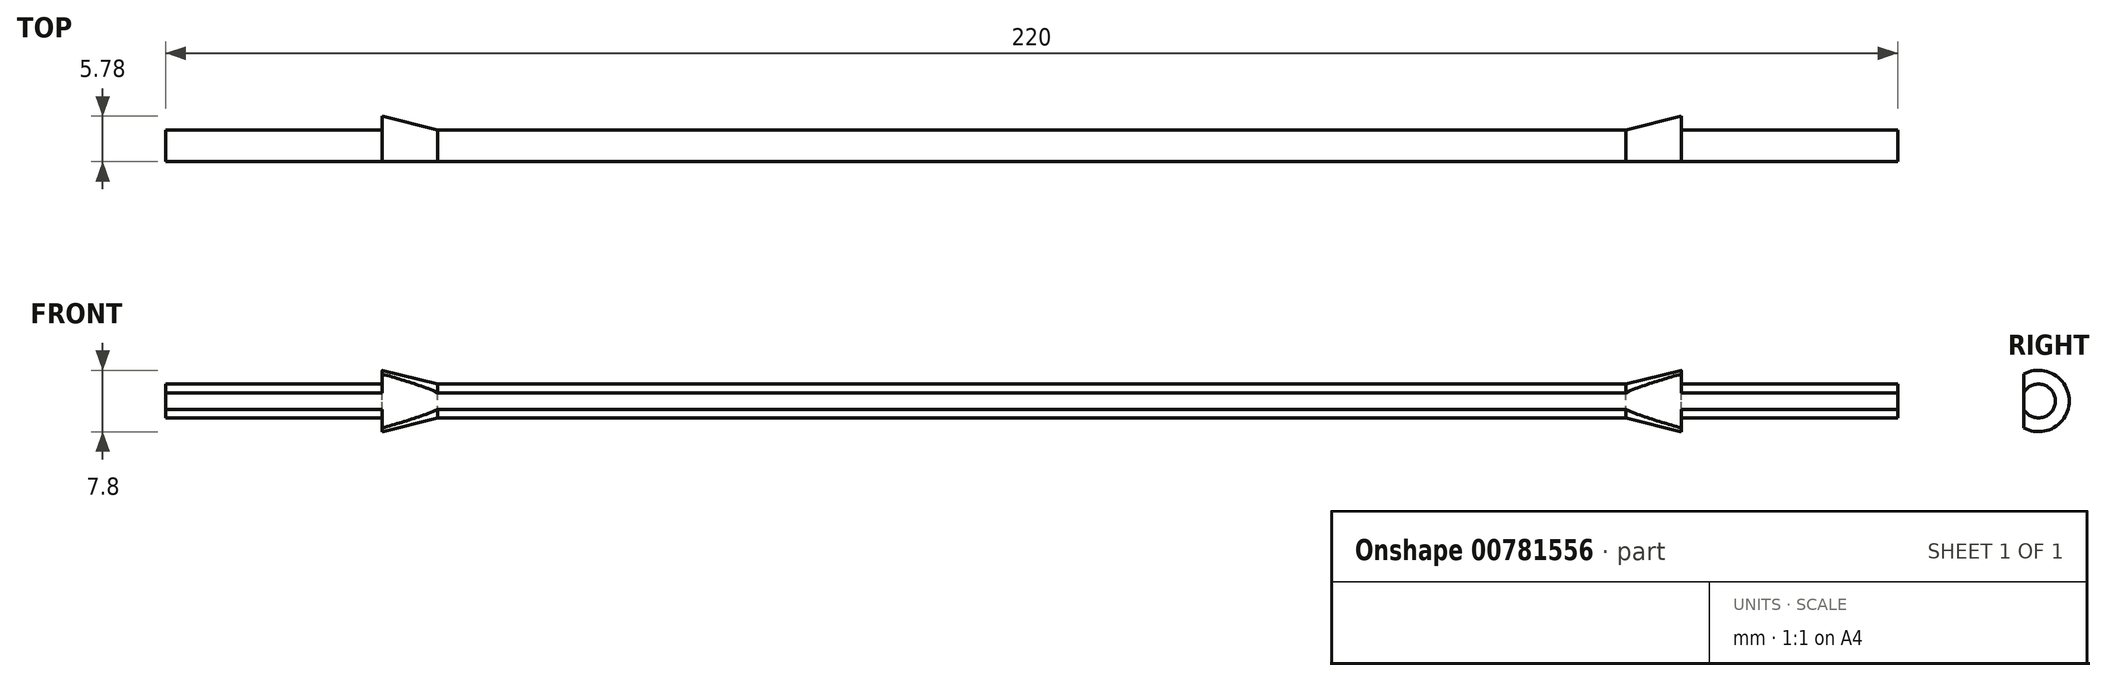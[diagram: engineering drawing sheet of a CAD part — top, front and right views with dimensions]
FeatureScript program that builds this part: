
annotation { "Feature Type Name" : "Feature", "Feature Type Description" : "" }
export const myFeature = defineFeature(function(context is Context, id is Id, definition is map)
    precondition{}
    {
        {
            var Q0;
            Q0=qCreatedBy(makeId("Top.planeOp"),FACE);
            var sketch = newSketch(context, id + "F0", { "sketchPlane" : qUnion([Q0])});
            skLineSegment(sketch, "E0.bottom", {"start": v(-123.69, -1.75) * mm, "end": v(96.31, -1.75) * mm});
            skLineSegment(sketch, "E0.top", {"start": v(-123.69, -6.05) * mm, "end": v(96.31, -6.05) * mm});
            skLineSegment(sketch, "E0.left", {"start": v(-123.69, -1.75) * mm, "end": v(-123.69, -6.05) * mm});
            skLineSegment(sketch, "E0.right", {"start": v(96.31, -1.75) * mm, "end": v(96.31, -6.05) * mm});
            skPoint(sketch, "E1", {"position": v(-13.69, -6.05) * mm});
            skLineSegment(sketch, "E2", {"start": v(-96.19, -7.8) * mm, "end": v(-96.19, 0) * mm});
            skPoint(sketch, "E3", {"position": v(-123.69, -3.9) * mm});
            skPoint(sketch, "E4", {"position": v(96.31, -3.9) * mm});
            skLineSegment(sketch, "E5", {"start": v(96.31, -3.9) * mm, "end": v(-123.69, -3.9) * mm});
            skPoint(sketch, "E6", {"position": v(-96.19, -3.9) * mm});
            skLineSegment(sketch, "E7", {"start": v(-96.19, 0) * mm, "end": v(-80.53, -3.9) * mm});
            skLineSegment(sketch, "E8", {"start": v(-80.53, -3.9) * mm, "end": v(-96.19, -7.8) * mm});
            skLineSegment(sketch, "E9", {"start": v(68.81, 0) * mm, "end": v(68.81, -7.8) * mm});
            skPoint(sketch, "E10", {"position": v(68.81, -3.9) * mm});
            skLineSegment(sketch, "E11", {"start": v(68.81, -7.8) * mm, "end": v(53.15, -3.9) * mm});
            skLineSegment(sketch, "E12", {"start": v(53.15, -3.9) * mm, "end": v(68.81, 0) * mm});
            skLineSegment(sketch, "E13", {"start": v(-123.69, -3.9) * mm, "end": v(-96.19, -3.9) * mm});
            skLineSegment(sketch, "E14", {"start": v(68.81, -3.9) * mm, "end": v(96.31, -3.9) * mm});
            skSolve(sketch);
        }
        {
            var Q0;
            {var subQ0=sQuery(id+"F0.wireOp",EDGE,"E7");var subQ1=sQuery(id+"F0.wireOp",EDGE,"E0.bottom");var subQ2=makeQuery(id+"F0.imprint","INTERSECT",VERTEX,{"derivedFrom":[subQ1,subQ0]});Q0=makeQuery(id+"F0.imprint","IMPRINT",FACE,{"disambiguationData":[TD([[makeQuery(id+"F0.imprint","IMPRINT",EDGE,{"disambiguationData":[TD([[subQ2,-1.0]])],"derivedFrom":subQ1}),-1.0]])]});}
            var Q1;
            {var subQ0=sQuery(id+"F0.wireOp",EDGE,"E7");var subQ1=sQuery(id+"F0.wireOp",EDGE,"E0.bottom");var subQ2=makeQuery(id+"F0.imprint","INTERSECT",VERTEX,{"derivedFrom":[subQ1,subQ0]});Q1=makeQuery(id+"F0.imprint","IMPRINT",FACE,{"disambiguationData":[TD([[makeQuery(id+"F0.imprint","IMPRINT",EDGE,{"disambiguationData":[TD([[subQ2,1.0]])],"derivedFrom":subQ1}),-1.0]])]});}
            var Q2;
            {var subQ0=sQuery(id+"F0.wireOp",EDGE,"E7");var subQ1=sQuery(id+"F0.wireOp",EDGE,"E0.bottom");var subQ2=makeQuery(id+"F0.imprint","INTERSECT",VERTEX,{"derivedFrom":[subQ1,subQ0]});Q2=makeQuery(id+"F0.imprint","IMPRINT",FACE,{"disambiguationData":[TD([[makeQuery(id+"F0.imprint","IMPRINT",EDGE,{"disambiguationData":[TD([[subQ2,1.0]])],"derivedFrom":subQ1}),1.0]])]});}
            var Q3;
            {var subQ0=sQuery(id+"F0.wireOp",EDGE,"E0.left");var subQ1=sQuery(id+"F0.wireOp",EDGE,"E0.bottom");var subQ2=makeQuery(id+"F0.imprint","INTERSECT",VERTEX,{"derivedFrom":[subQ1,subQ0]});Q3=makeQuery(id+"F0.imprint","IMPRINT",FACE,{"disambiguationData":[TD([[makeQuery(id+"F0.imprint","IMPRINT",EDGE,{"disambiguationData":[TD([[subQ2,-1.0]])],"derivedFrom":subQ1}),-1.0]])]});}
            var Q4;
            {var subQ0=sQuery(id+"F0.wireOp",EDGE,"E9");var subQ1=sQuery(id+"F0.wireOp",EDGE,"E0.bottom");var subQ2=makeQuery(id+"F0.imprint","INTERSECT",VERTEX,{"derivedFrom":[subQ1,subQ0]});Q4=makeQuery(id+"F0.imprint","IMPRINT",FACE,{"disambiguationData":[TD([[makeQuery(id+"F0.imprint","IMPRINT",EDGE,{"disambiguationData":[TD([[subQ2,1.0]])],"derivedFrom":subQ1}),-1.0]])]});}
            var Q5;
            {var subQ0=sQuery(id+"F0.wireOp",EDGE,"E9");var subQ1=sQuery(id+"F0.wireOp",EDGE,"E0.bottom");var subQ2=makeQuery(id+"F0.imprint","INTERSECT",VERTEX,{"derivedFrom":[subQ1,subQ0]});Q5=makeQuery(id+"F0.imprint","IMPRINT",FACE,{"disambiguationData":[TD([[makeQuery(id+"F0.imprint","IMPRINT",EDGE,{"disambiguationData":[TD([[subQ2,1.0]])],"derivedFrom":subQ1}),1.0]])]});}
            var Q6;
            {var subQ0=sQuery(id+"F0.wireOp",EDGE,"E9");var subQ1=sQuery(id+"F0.wireOp",EDGE,"E0.bottom");var subQ2=makeQuery(id+"F0.imprint","INTERSECT",VERTEX,{"derivedFrom":[subQ1,subQ0]});Q6=makeQuery(id+"F0.imprint","IMPRINT",FACE,{"disambiguationData":[TD([[makeQuery(id+"F0.imprint","IMPRINT",EDGE,{"disambiguationData":[TD([[subQ2,-1.0]])],"derivedFrom":subQ1}),-1.0]])]});}
            var Q7;
            Q7=sQuery(id+"F0.wireOp",EDGE,"E5");
            revolve(context, id + "F1", {"surfaceOperationType" : NewSurfaceOperationType.NEW, "entities" : qUnion([Q0, Q1, Q2, Q3, Q4, Q5, Q6]), "axis" : qUnion([Q7]), "revolveType" : RevolveType.FULL});
        }
        {
            var Q0;
            Q0=makeQuery(id+"F1.opRevolve","SWEPT_FACE",FACE,{"disambiguationData":[OSD([sQuery(id+"F0.wireOp",EDGE,"E0.left")])]});
            var sketch = newSketch(context, id + "F2", { "sketchPlane" : qUnion([Q0])});
            skCircle(sketch, "E15.0.0", {"center": v(3.9, 0) * mm, "radius": 2.15 * mm});
            skCircle(sketch, "E16.0", {"center": v(3.9, 0) * mm, "radius": 3.9 * mm});
            skLineSegment(sketch, "E17.bottom", {"start": v(0, 0) * mm, "end": v(0, 0) * mm});
            skLineSegment(sketch, "E17.top", {"start": v(0, 0) * mm, "end": v(0, 0) * mm});
            skLineSegment(sketch, "E17.left", {"start": v(0, 0) * mm, "end": v(0, 0) * mm});
            skLineSegment(sketch, "E17.right", {"start": v(0, 0) * mm, "end": v(0, 0) * mm});
            skLineSegment(sketch, "E18", {"start": v(6.05, -6.66) * mm, "end": v(6.05, 11.88) * mm});
            skLineSegment(sketch, "E19.bottom", {"start": v(6.05, -6.66) * mm, "end": v(-5.02, -6.66) * mm});
            skLineSegment(sketch, "E19.top", {"start": v(6.05, 9.42) * mm, "end": v(-5.02, 9.42) * mm});
            skLineSegment(sketch, "E19.left", {"start": v(6.05, -6.66) * mm, "end": v(6.05, 9.42) * mm});
            skLineSegment(sketch, "E19.right", {"start": v(-5.02, -6.66) * mm, "end": v(-5.02, 9.42) * mm});
            skLineSegment(sketch, "E20", {"start": v(5.78, -6.66) * mm, "end": v(5.78, 9.42) * mm});
            skSolve(sketch);
        }
        {
            var Q0;
            {var subQ0=sQuery(id+"F2.wireOp",EDGE,"E19.right");Q0=makeQuery(id+"F2.imprint","IMPRINT",FACE,{"disambiguationData":[TD([[makeQuery(id+"F2.imprint","IMPRINT",EDGE,{"derivedFrom":subQ0}),-1.0]])]});}
            var Q1;
            {var subQ0=sQuery(id+"F2.wireOp",EDGE,"E20");var subQ1=sQuery(id+"F2.wireOp",EDGE,"E15.0.0");var subQ2=makeQuery(id+"F2.imprint","INTERSECT",VERTEX,{"disambiguationData":[OD(0.0)],"derivedFrom":[subQ1,subQ0]});Q1=makeQuery(id+"F2.imprint","IMPRINT",FACE,{"disambiguationData":[TD([[makeQuery(id+"F2.imprint","IMPRINT",EDGE,{"disambiguationData":[TD([[subQ2,1.0]])],"derivedFrom":subQ1}),1.0]])]});}
            var Q2;
            {var subQ0=sQuery(id+"F2.wireOp",EDGE,"E20");var subQ1=sQuery(id+"F2.wireOp",EDGE,"E15.0.0");var subQ2=makeQuery(id+"F2.imprint","INTERSECT",VERTEX,{"disambiguationData":[OD(0.0)],"derivedFrom":[subQ1,subQ0]});Q2=makeQuery(id+"F2.imprint","IMPRINT",FACE,{"disambiguationData":[TD([[makeQuery(id+"F2.imprint","IMPRINT",EDGE,{"disambiguationData":[TD([[subQ2,1.0]])],"derivedFrom":subQ1}),-1.0]])]});}
            var Q3;
            Q3=makeQuery(id+"F1.opRevolve","SWEPT_FACE",FACE,{"disambiguationData":[OSD([sQuery(id+"F0.wireOp",EDGE,"E0.right")])]});
            extrude(context, id + "F3", {"entities" : qUnion([Q0, Q1, Q2]), "operationType" : NewBodyOperationType.INTERSECT, "depth" : 25 * mm, "offsetDistance" : 25 * mm, "hasSecondDirection" : true, "secondDirectionBound" : SecondDirectionBoundingType.UP_TO_SURFACE, "secondDirectionOppositeDirection" : true, "secondDirectionDepth" : 25 * mm, "secondDirectionBoundEntityFace" : qUnion([Q3])});
        }
    });
